# Revit family: Sanitary_Wash-Basins_hansgrohe_60319XXX-Xelu-Q-Handrinse-basin-with-shelf-right-800-480_NEW
name_source: partatom
category: Plumbing Fixtures
units: mm (PartAtom-declared; Revit-internal decimal feet)

## family parameters
Cut with Voids When Loaded = Yes
Host = Face
Maintain Annotation Orientation = No
OmniClass Number = 23.31.13.00
OmniClass Title = Sinks
Part Type = Normal
Room Calculation Point = No
Round Connector Dimension = Use Diameter
Shared = No

## types (1)
- 60319XXX Xelu Q Wash basin with shelf right 800/480 with 2 tap holes without overflow
    Connector Description = Water Outlet 46 mm
    Default Elevation = 0 mm  [stored 0 ft]
    Description = Xelu Q Wash basin with shelf right 800/480 with 2 tap holes without overflow
    Diameter = 46 mm  [stored 0.150919 ft]
    Manufacturer = Hansgrohe
    Material 1 = Hansgrohe - Ceramic - 450 White
    Model = 60319XXX
    Product Page URL = https://www.hansgrohe.com
    Product data url = https://bimobject.com
    URL = https://www.hansgrohe.com
    Version = 1

note: [stored X ft] marks values corroborated as IEEE doubles in the binary element streams (Revit-internal decimal feet)

## geometry (parser evidence)
native form markers: Sweep x5
no freeform markers — native parametric forms only
